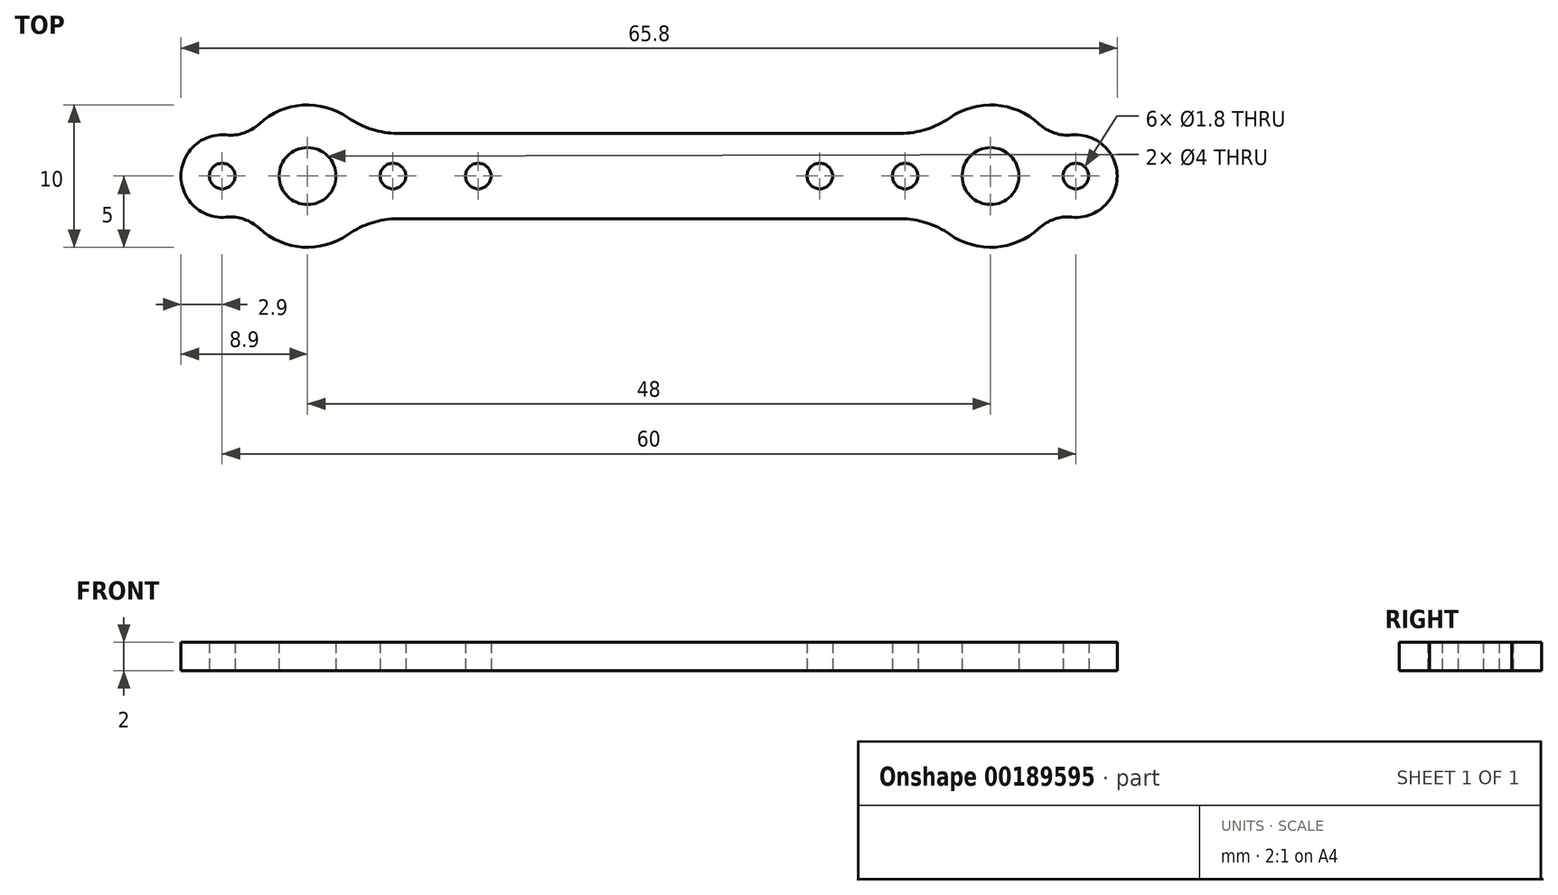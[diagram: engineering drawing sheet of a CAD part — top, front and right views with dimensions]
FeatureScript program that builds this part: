
annotation { "Feature Type Name" : "Feature", "Feature Type Description" : "" }
export const myFeature = defineFeature(function(context is Context, id is Id, definition is map)
    precondition{}
    {
        {
            var Q0;
            Q0=qCreatedBy(makeId("Top.planeOp"),FACE);
            var sketch = newSketch(context, id + "F0", { "sketchPlane" : qUnion([Q0])});
            skLineSegment(sketch, "E0", {"start": v(-24, 0) * mm, "end": v(0, 0) * mm, "construction": true});
            skCircle(sketch, "E1", {"center": v(-24, 0) * mm, "radius": 2 * mm});
            skCircle(sketch, "E2", {"center": v(-18, 0) * mm, "radius": 0.9 * mm});
            skCircle(sketch, "E3", {"center": v(-12, 0) * mm, "radius": 0.9 * mm});
            skCircle(sketch, "E4", {"center": v(-30, 0) * mm, "radius": 0.9 * mm});
            skLineSegment(sketch, "E5", {"start": v(0, -3) * mm, "end": v(-17.68, -3) * mm});
            skLineSegment(sketch, "E6.MirrorCS", {"start": v(0, 3) * mm, "end": v(-17.68, 3) * mm});
            skArc(sketch, "E7.0", {"start": v(-27.4, -3.67) * mm, "mid": v(-24.33, -4.99) * mm, "end": v(-21.13, -4.1) * mm});
            skArc(sketch, "E8.0", {"start": v(-29.72, 2.89) * mm, "mid": v(-32.9, 0) * mm, "end": v(-29.72, -2.89) * mm});
            skArc(sketch, "E9.trimOffspring", {"start": v(-21.13, 4.1) * mm, "mid": v(-24.33, 4.99) * mm, "end": v(-27.4, 3.67) * mm});
            skPoint(sketch, "E10.orphan", {"position": v(-20.26, -3) * mm});
            skPoint(sketch, "E11.orphan", {"position": v(-20.26, 3) * mm});
            skPoint(sketch, "E12.visualSharp", {"position": v(-20, 3) * mm});
            skArc(sketch, "E12.filletArc", {"start": v(-21.13, 4.1) * mm, "mid": v(-19.48, 3.28) * mm, "end": v(-17.68, 3) * mm});
            skPoint(sketch, "E13.visualSharp", {"position": v(-20, -3) * mm});
            skArc(sketch, "E13.filletArc", {"start": v(-17.68, -3) * mm, "mid": v(-19.48, -3.28) * mm, "end": v(-21.13, -4.1) * mm});
            skPoint(sketch, "E14.visualSharp", {"position": v(-28.38, 2.4) * mm});
            skArc(sketch, "E14.filletArc", {"start": v(-29.72, 2.89) * mm, "mid": v(-28.47, 3.03) * mm, "end": v(-27.4, 3.67) * mm});
            skPoint(sketch, "E15.visualSharp", {"position": v(-28.38, -2.4) * mm});
            skArc(sketch, "E15.filletArc", {"start": v(-27.4, -3.67) * mm, "mid": v(-28.47, -3.03) * mm, "end": v(-29.72, -2.89) * mm});
            skLineSegment(sketch, "E16", {"start": v(0, 0) * mm, "end": v(0, 10.38) * mm, "construction": true});
            skLineSegment(sketch, "E17.MirrorCS", {"start": v(0, 3) * mm, "end": v(17.68, 3) * mm});
            skLineSegment(sketch, "E18.MirrorCS", {"start": v(0, -3) * mm, "end": v(17.68, -3) * mm});
            skCircle(sketch, "E19.MirrorC", {"center": v(12, 0) * mm, "radius": 0.9 * mm});
            skCircle(sketch, "E20.MirrorC", {"center": v(18, 0) * mm, "radius": 0.9 * mm});
            skArc(sketch, "E21.MirrorCS", {"start": v(17.68, -3) * mm, "mid": v(19.48, -3.28) * mm, "end": v(21.13, -4.1) * mm});
            skArc(sketch, "E22.MirrorCS", {"start": v(27.4, -3.67) * mm, "mid": v(24.33, -4.99) * mm, "end": v(21.13, -4.1) * mm});
            skArc(sketch, "E23.MirrorCS", {"start": v(27.4, -3.67) * mm, "mid": v(28.47, -3.03) * mm, "end": v(29.72, -2.89) * mm});
            skArc(sketch, "E24.MirrorCS", {"start": v(29.72, 2.89) * mm, "mid": v(32.9, 0) * mm, "end": v(29.72, -2.89) * mm});
            skArc(sketch, "E25.MirrorCS", {"start": v(29.72, 2.89) * mm, "mid": v(28.47, 3.03) * mm, "end": v(27.4, 3.67) * mm});
            skArc(sketch, "E26.MirrorCS", {"start": v(21.13, 4.1) * mm, "mid": v(24.33, 4.99) * mm, "end": v(27.4, 3.67) * mm});
            skArc(sketch, "E27.MirrorCS", {"start": v(21.13, 4.1) * mm, "mid": v(19.48, 3.28) * mm, "end": v(17.68, 3) * mm});
            skCircle(sketch, "E28.MirrorC", {"center": v(24, 0) * mm, "radius": 2 * mm});
            skCircle(sketch, "E29.MirrorC", {"center": v(30, 0) * mm, "radius": 0.9 * mm});
            skSolve(sketch);
        }
        {
            var Q0;
            Q0=makeQuery(id+"F0.imprint","IMPRINT",FACE,{"disambiguationData":[TD([[makeQuery(id+"F0.imprint","IMPRINT",EDGE,{"derivedFrom":sQuery(id+"F0.wireOp",EDGE,"E1")}),-1.0]])]});
            extrude(context, id + "F1", {"entities" : qUnion([Q0]), "depth" : 2 * mm});
        }
    });
